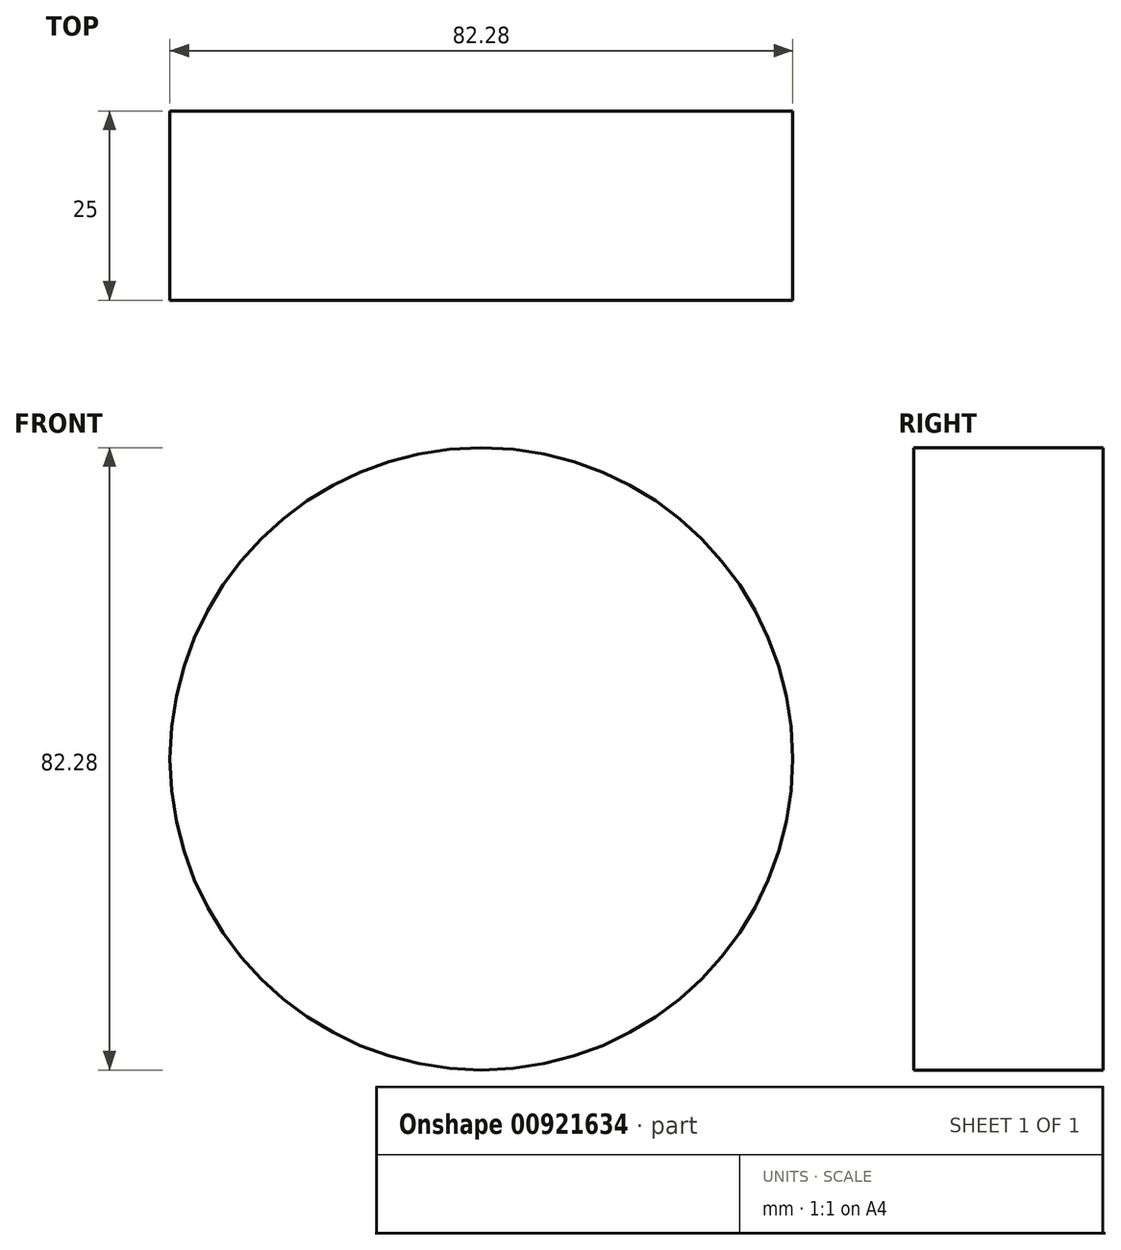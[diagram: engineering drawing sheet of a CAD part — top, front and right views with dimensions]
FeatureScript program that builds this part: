
annotation { "Feature Type Name" : "Feature", "Feature Type Description" : "" }
export const myFeature = defineFeature(function(context is Context, id is Id, definition is map)
    precondition{}
    {
        {
            var Q0;
            Q0=qCreatedBy(makeId("Front.planeOp"),FACE);
            var sketch = newSketch(context, id + "F0", { "sketchPlane" : qUnion([Q0])});
            skCircle(sketch, "E0", {"center": v(0, 0) * mm, "radius": 41.14 * mm});
            skSolve(sketch);
        }
        {
            var Q0;
            Q0=makeQuery(id+"F0.imprint","IMPRINT",FACE,{"disambiguationData":[TD([[makeQuery(id+"F0.imprint","IMPRINT",EDGE,{"derivedFrom":sQuery(id+"F0.wireOp",EDGE,"E0")}),1.0]])]});
            var Q1;
            Q1 = qSketchRegion(id + "F0", true);
            extrude(context, id + "F1", {"entities" : qUnion([Q0, Q1]), "depth" : 25 * mm, "offsetDistance" : 25 * mm});
        }
    });
